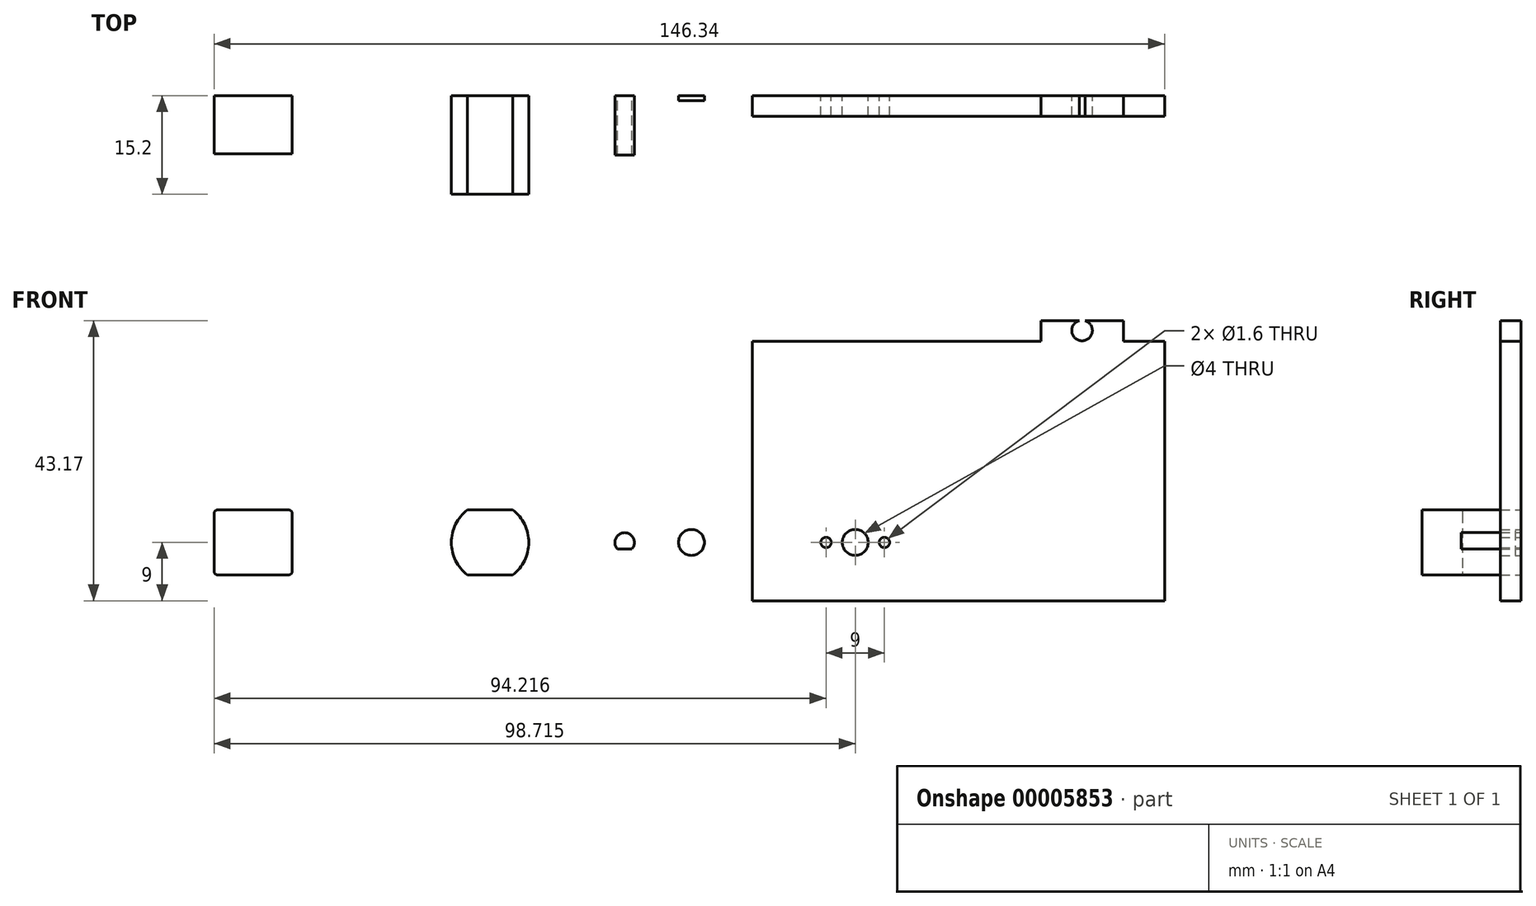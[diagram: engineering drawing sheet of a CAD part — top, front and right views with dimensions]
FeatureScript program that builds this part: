
annotation { "Feature Type Name" : "Feature", "Feature Type Description" : "" }
export const myFeature = defineFeature(function(context is Context, id is Id, definition is map)
    precondition{}
    {
        {
            var Q0;
            Q0=qCreatedBy(makeId("Front.planeOp"),FACE);
            var sketch = newSketch(context, id + "F0", { "sketchPlane" : qUnion([Q0])});
            skArc(sketch, "E0", {"start": v(1.12, -1) * mm, "mid": v(0, 1.5) * mm, "end": v(-1.12, -1) * mm});
            skLineSegment(sketch, "E1", {"start": v(-1.12, -1) * mm, "end": v(1.12, -1) * mm});
            skPoint(sketch, "E2.orphan", {"position": v(0, 1.5) * mm});
            skPoint(sketch, "E3.end.orphan", {"position": v(0, -1) * mm});
            skLineSegment(sketch, "E4.bottom", {"start": v(-62.7, 5) * mm, "end": v(-51.72, 5) * mm});
            skLineSegment(sketch, "E4.top", {"start": v(-62.7, -5) * mm, "end": v(-51.72, -5) * mm});
            skLineSegment(sketch, "E4.left", {"start": v(-63.21, 4.5) * mm, "end": v(-63.21, -4.5) * mm});
            skLineSegment(sketch, "E4.right", {"start": v(-51.21, 4.5) * mm, "end": v(-51.21, -4.5) * mm});
            skPoint(sketch, "E5.visualSharp", {"position": v(-51.21, 5) * mm});
            skArc(sketch, "E5.filletArc", {"start": v(-51.21, 4.5) * mm, "mid": v(-51.36, 4.85) * mm, "end": v(-51.72, 5) * mm});
            skPoint(sketch, "E6.visualSharp", {"position": v(-63.21, 5) * mm});
            skArc(sketch, "E6.filletArc", {"start": v(-62.7, 5) * mm, "mid": v(-63.06, 4.85) * mm, "end": v(-63.21, 4.5) * mm});
            skPoint(sketch, "E7.visualSharp", {"position": v(-63.21, -5) * mm});
            skArc(sketch, "E7.filletArc", {"start": v(-63.21, -4.5) * mm, "mid": v(-63.06, -4.85) * mm, "end": v(-62.7, -5) * mm});
            skPoint(sketch, "E8.visualSharp", {"position": v(-51.21, -5) * mm});
            skArc(sketch, "E8.filletArc", {"start": v(-51.72, -5) * mm, "mid": v(-51.36, -4.85) * mm, "end": v(-51.21, -4.5) * mm});
            skLineSegment(sketch, "E9", {"start": v(-57.21, 5) * mm, "end": v(-57.21, 2) * mm, "construction": true});
            skCircle(sketch, "E10", {"center": v(-57.21, 0) * mm, "radius": 2 * mm, "construction": true});
            skArc(sketch, "E11", {"start": v(-58.33, 1) * mm, "mid": v(-57.21, -1.5) * mm, "end": v(-56.1, 1) * mm, "construction": true});
            skLineSegment(sketch, "E12", {"start": v(-58.33, 1) * mm, "end": v(-56.1, 1) * mm, "construction": true});
            skLineSegment(sketch, "E13", {"start": v(-57.21, 0) * mm, "end": v(-52.71, 0) * mm, "construction": true});
            skLineSegment(sketch, "E14", {"start": v(-57.21, 0) * mm, "end": v(-61.71, 0) * mm, "construction": true});
            skCircle(sketch, "E15", {"center": v(-61.71, 0) * mm, "radius": 0.8 * mm, "construction": true});
            skCircle(sketch, "E16", {"center": v(-52.71, 0) * mm, "radius": 0.8 * mm, "construction": true});
            skLineSegment(sketch, "E17.bottom", {"start": v(-24.22, 5) * mm, "end": v(-17.22, 5) * mm});
            skLineSegment(sketch, "E17.top", {"start": v(-24.22, -5) * mm, "end": v(-17.22, -5) * mm});
            skArc(sketch, "E18", {"start": v(-24.22, 5) * mm, "mid": v(-26.68, 0) * mm, "end": v(-24.22, -5) * mm});
            skArc(sketch, "E19.0.MirrorCS", {"start": v(-17.22, 5) * mm, "mid": v(-14.76, 0) * mm, "end": v(-17.22, -5) * mm});
            skPoint(sketch, "E20.orphan", {"position": v(-26.72, 5) * mm});
            skCircle(sketch, "E21", {"center": v(10.29, 0) * mm, "radius": 2 * mm});
            skLineSegment(sketch, "E22.bottom", {"start": v(19.63, 31) * mm, "end": v(64.08, 31) * mm});
            skLineSegment(sketch, "E22.top", {"start": v(19.63, -9) * mm, "end": v(83.13, -9) * mm});
            skLineSegment(sketch, "E22.left", {"start": v(19.63, 31) * mm, "end": v(19.63, -9) * mm});
            skLineSegment(sketch, "E22.right", {"start": v(83.13, 31) * mm, "end": v(83.13, -9) * mm});
            skCircle(sketch, "E23", {"center": v(35.5, 0) * mm, "radius": 2 * mm});
            skCircle(sketch, "E24", {"center": v(40, 0) * mm, "radius": 0.8 * mm});
            skCircle(sketch, "E25", {"center": v(31, 0) * mm, "radius": 0.8 * mm});
            skLineSegment(sketch, "E26.top", {"start": v(76.78, 34.18) * mm, "end": v(64.08, 34.18) * mm});
            skLineSegment(sketch, "E26.left", {"start": v(76.78, 31) * mm, "end": v(76.78, 34.18) * mm});
            skLineSegment(sketch, "E26.right", {"start": v(64.08, 31) * mm, "end": v(64.08, 34.18) * mm});
            skLineSegment(sketch, "E27.trimOffspring", {"start": v(76.78, 31) * mm, "end": v(83.13, 31) * mm});
            skLineSegment(sketch, "E28", {"start": v(70.43, 34.18) * mm, "end": v(70.43, 32.65) * mm});
            skCircle(sketch, "E29", {"center": v(70.43, 32.65) * mm, "radius": 1.59 * mm});
            skSolve(sketch);
        }
        {
            var Q0;
            Q0=makeQuery(id+"F0.imprint","IMPRINT",FACE,{"disambiguationData":[TD([[makeQuery(id+"F0.imprint","IMPRINT",EDGE,{"derivedFrom":sQuery(id+"F0.wireOp",EDGE,"E0")}),1.0]])]});
            extrude(context, id + "F1", {"entities" : qUnion([Q0]), "depth" : 9.2 * mm});
        }
        {
            var Q0;
            Q0=makeQuery(id+"F0.imprint","IMPRINT",FACE,{"disambiguationData":[TD([[makeQuery(id+"F0.imprint","IMPRINT",EDGE,{"derivedFrom":sQuery(id+"F0.wireOp",EDGE,"E0")}),1.0]])]});
            var Q1;
            Q1=makeQuery(id+"F0.imprint","IMPRINT",FACE,{"disambiguationData":[TD([[makeQuery(id+"F0.imprint","IMPRINT",EDGE,{"derivedFrom":sQuery(id+"F0.wireOp",EDGE,"E4.bottom")}),-1.0]])]});
            var Q2;
            {var subQ1=sQuery(id+"F0.wireOp",EDGE,"f48740dc-65db-413f-936f-9fc325a0c46d.left");Q2=makeQuery(id+"F0.imprint","IMPRINT",FACE,{"disambiguationData":[TD([[makeQuery(id+"F0.imprint","IMPRINT",EDGE,{"derivedFrom":subQ1}),-1.0]])]});}
            var Q3;
            {var subQ1=sQuery(id+"F0.wireOp",EDGE,"f48740dc-65db-413f-936f-9fc325a0c46d.right");Q3=makeQuery(id+"F0.imprint","IMPRINT",FACE,{"disambiguationData":[TD([[makeQuery(id+"F0.imprint","IMPRINT",EDGE,{"derivedFrom":subQ1}),1.0]])]});}
            extrude(context, id + "F2", {"entities" : qUnion([Q0, Q1, Q2, Q3]), "operationType" : NewBodyOperationType.ADD, "depth" : 9 * mm});
        }
        {
            var Q0;
            Q0=makeQuery(id+"F0.imprint","IMPRINT",FACE,{"disambiguationData":[TD([[makeQuery(id+"F0.imprint","IMPRINT",EDGE,{"derivedFrom":sQuery(id+"F0.wireOp",EDGE,"E17.bottom")}),-1.0]])]});
            extrude(context, id + "F3", {"entities" : qUnion([Q0]), "depth" : 15.2 * mm});
        }
        {
            var Q0;
            Q0=makeQuery(id+"F0.imprint","IMPRINT",FACE,{"disambiguationData":[TD([[makeQuery(id+"F0.imprint","IMPRINT",EDGE,{"derivedFrom":sQuery(id+"F0.wireOp",EDGE,"E21")}),1.0]])]});
            extrude(context, id + "F4", {"entities" : qUnion([Q0]), "depth" : 0.8 * mm});
        }
        {
            var Q0;
            Q0=makeQuery(id+"F0.imprint","IMPRINT",FACE,{"disambiguationData":[TD([[makeQuery(id+"F0.imprint","IMPRINT",EDGE,{"derivedFrom":sQuery(id+"F0.wireOp",EDGE,"E22.bottom")}),-1.0]])]});
            extrude(context, id + "F5", {"entities" : qUnion([Q0]), "depth" : 3.17 * mm});
        }
    });
